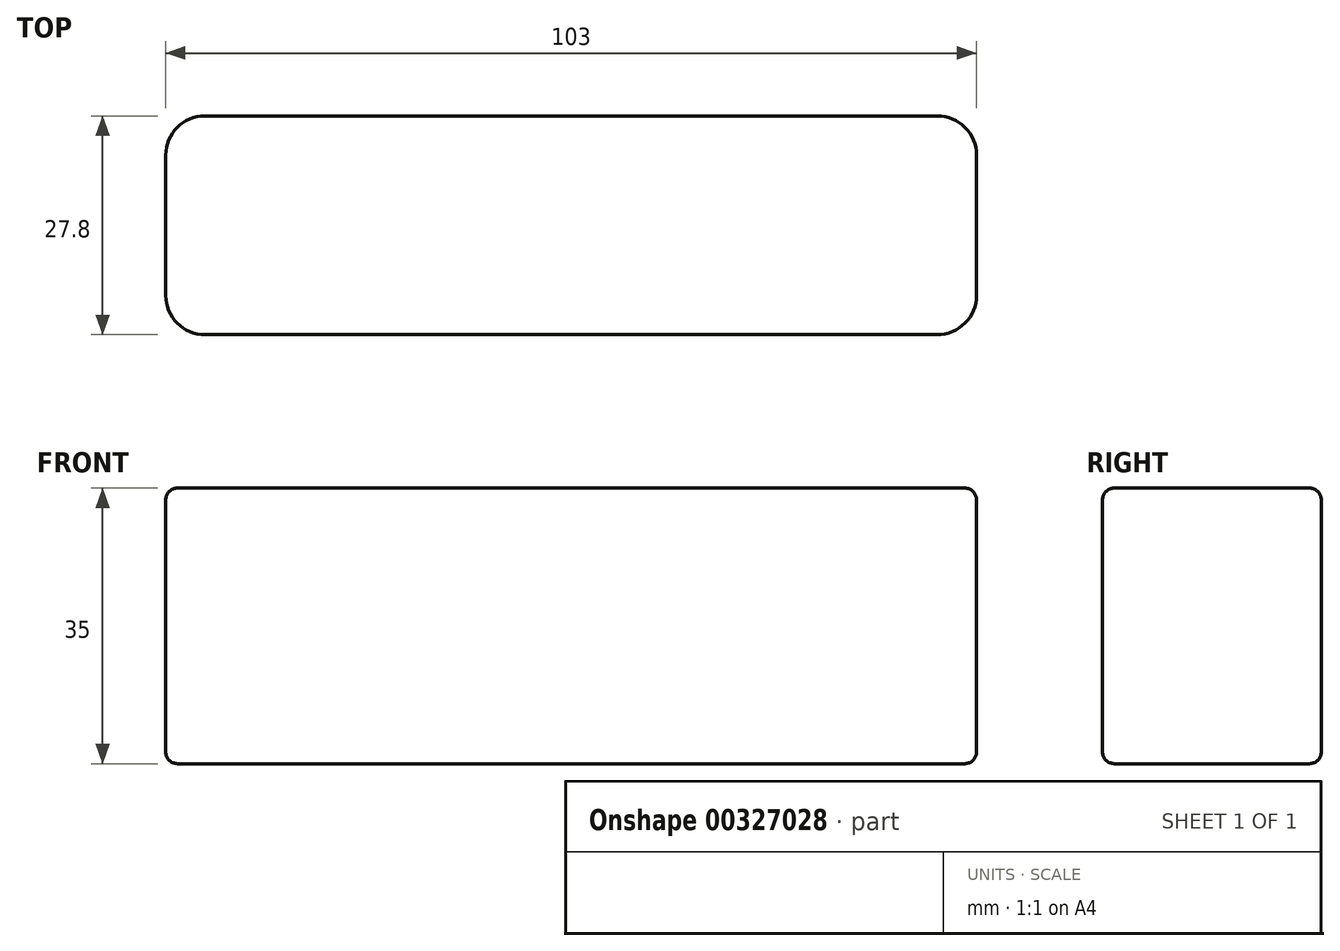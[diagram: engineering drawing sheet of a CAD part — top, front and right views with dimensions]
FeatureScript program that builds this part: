
annotation { "Feature Type Name" : "Feature", "Feature Type Description" : "" }
export const myFeature = defineFeature(function(context is Context, id is Id, definition is map)
    precondition{}
    {
        {
            var Q0;
            Q0=qCreatedBy(makeId("Top.planeOp"),FACE);
            var sketch = newSketch(context, id + "F0", { "sketchPlane" : qUnion([Q0])});
            skLineSegment(sketch, "E0.bottom", {"start": v(51.5, 13.9) * mm, "end": v(-51.5, 13.9) * mm});
            skLineSegment(sketch, "E0.top", {"start": v(51.5, -13.9) * mm, "end": v(-51.5, -13.9) * mm});
            skLineSegment(sketch, "E0.left", {"start": v(51.5, 13.9) * mm, "end": v(51.5, -13.9) * mm});
            skLineSegment(sketch, "E0.right", {"start": v(-51.5, 13.9) * mm, "end": v(-51.5, -13.9) * mm});
            skPoint(sketch, "E0.middle", {"position": v(0, 0) * mm});
            skSolve(sketch);
        }
        {
            var Q0;
            Q0 = qSketchRegion(id + "F0", true);
            extrude(context, id + "F1", {"entities" : qUnion([Q0]), "depth" : 35 * mm});
        }
        {
            var Q0;
            Q0=makeQuery(id+"F1.opExtrude","SWEPT_EDGE",EDGE,{"disambiguationData":[OSD([sQuery(id+"F0.wireOp",EDGE,"E0.top"),sQuery(id+"F0.wireOp",EDGE,"E0.right")])]});
            var Q1;
            Q1=makeQuery(id+"F1.opExtrude","SWEPT_EDGE",EDGE,{"disambiguationData":[OSD([sQuery(id+"F0.wireOp",EDGE,"E0.bottom"),sQuery(id+"F0.wireOp",EDGE,"E0.right")])]});
            var Q2;
            Q2=makeQuery(id+"F1.opExtrude","SWEPT_EDGE",EDGE,{"disambiguationData":[OSD([sQuery(id+"F0.wireOp",EDGE,"E0.bottom"),sQuery(id+"F0.wireOp",EDGE,"E0.left")])]});
            var Q3;
            Q3=makeQuery(id+"F1.opExtrude","SWEPT_EDGE",EDGE,{"disambiguationData":[OSD([sQuery(id+"F0.wireOp",EDGE,"E0.top"),sQuery(id+"F0.wireOp",EDGE,"E0.left")])]});
            fillet(context, id + "F2", {"entities" : qUnion([Q0, Q1, Q2, Q3]), "radius" : 5 * mm, "tangentPropagation" : true, "allowEdgeOverflow" : false});
        }
        {
            var Q0;
            Q0=makeQuery(id+"F1.opExtrude","CAP_FACE",FACE,{"disambiguationData":[OSD([sQuery(id+"F0.wireOp",EDGE,"E0.bottom"),sQuery(id+"F0.wireOp",EDGE,"E0.top"),sQuery(id+"F0.wireOp",EDGE,"E0.left"),sQuery(id+"F0.wireOp",EDGE,"E0.right")])],"isStart":false});
            var Q1;
            Q1=makeQuery(id+"F1.opExtrude","CAP_FACE",FACE,{"disambiguationData":[OSD([sQuery(id+"F0.wireOp",EDGE,"E0.bottom"),sQuery(id+"F0.wireOp",EDGE,"E0.top"),sQuery(id+"F0.wireOp",EDGE,"E0.left"),sQuery(id+"F0.wireOp",EDGE,"E0.right")])],"isStart":true});
            fillet(context, id + "F3", {"entities" : qUnion([Q0, Q1]), "radius" : 1.5 * mm, "tangentPropagation" : true, "allowEdgeOverflow" : false});
        }
    });
